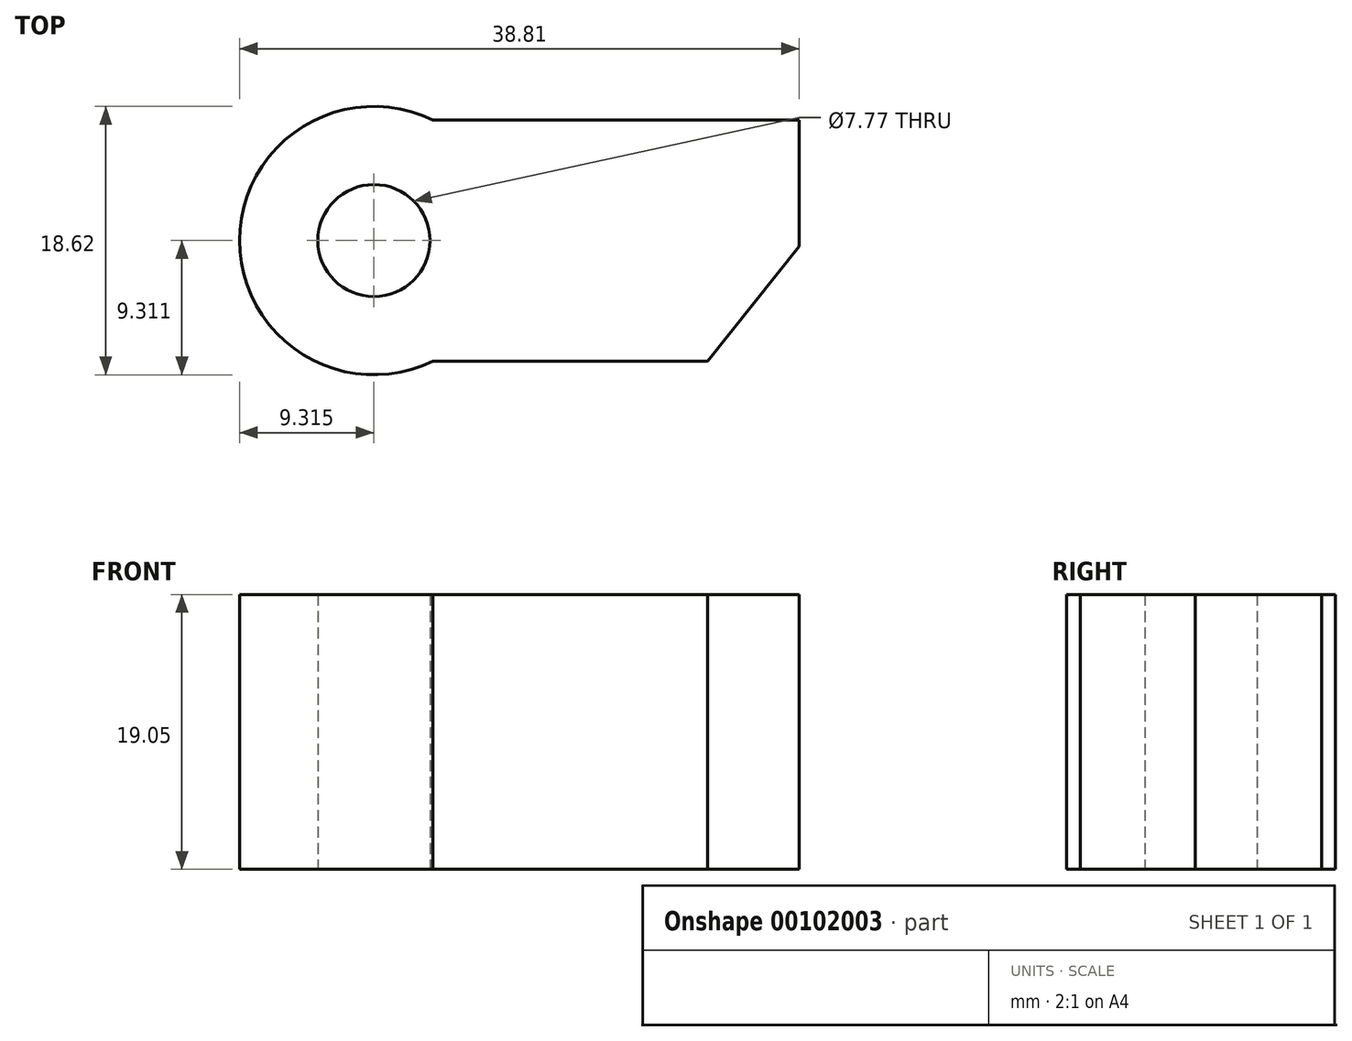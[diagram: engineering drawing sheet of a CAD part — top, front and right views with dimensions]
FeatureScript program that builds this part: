
annotation { "Feature Type Name" : "Feature", "Feature Type Description" : "" }
export const myFeature = defineFeature(function(context is Context, id is Id, definition is map)
    precondition{}
    {
        {
            var Q0;
            Q0=qCreatedBy(makeId("Top.planeOp"),FACE);
            var sketch = newSketch(context, id + "F0", { "sketchPlane" : qUnion([Q0])});
            skLineSegment(sketch, "E0", {"start": v(0, 0) * mm, "end": v(19.05, 0) * mm});
            skLineSegment(sketch, "E1", {"start": v(19.05, 0) * mm, "end": v(25.4, 7.95) * mm});
            skLineSegment(sketch, "E2", {"start": v(25.4, 7.95) * mm, "end": v(25.4, 16.72) * mm});
            skLineSegment(sketch, "E3", {"start": v(25.4, 16.72) * mm, "end": v(0, 16.72) * mm});
            skCircle(sketch, "E4", {"center": v(-4.1, 8.36) * mm, "radius": 9.31 * mm});
            skCircle(sketch, "E5", {"center": v(-4.1, 8.36) * mm, "radius": 3.89 * mm});
            skSolve(sketch);
        }
        {
            var Q0;
            Q0 = qSketchRegion(id + "F0", true);
            extrude(context, id + "F1", {"entities" : qUnion([Q0]), "depth" : 19.05 * mm});
        }
        {
            var Q0;
            Q0 = qSketchRegion(id + "F0", true);
            extrude(context, id + "F2", {"entities" : qUnion([Q0]), "operationType" : NewBodyOperationType.ADD, "depth" : 19.05 * mm});
        }
    });
